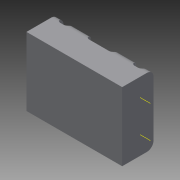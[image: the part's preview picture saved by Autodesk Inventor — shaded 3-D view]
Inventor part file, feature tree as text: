
AUTODESK INVENTOR PART (.ipt)
format: ipt  version: 2014 (Build 180170000, 170)  size: 228,864 bytes
history: native  units: mm
features: sketch x5, extrude x4, other x2, plane x1, fillet x1, shell x1, mirror x1
ambient origin geometry x8: Origin, YZ Plane, XZ Plane, XY Plane, X Axis, Y Axis, Z Axis, Center Point
bodies: Volumenkörper1 (feature_tree)
feature tree (15):
  extrude  "Extrusion1"  Depth=4.0mm
  plane  "Arbeitsebene1"
  fillet  "Rundung2"  Radius=19.0mm
  shell  "Hülle1"  Thickness=4.0mm
  extrude  "Extrusion2"  Depth=2.0mm
  mirror  "Spiegeln1"
  extrude  "Extrusion3"  Depth=2.0mm
  extrude  "Extrusion4"  Depth=2.0mm
  sketch  "Skizze5"  dims[d13=2.0mm d14=2.0mm d15=4.0mm d16=4.0mm d17=19.0mm d18=0.0mm d19=4.0mm d20=1.5mm d21=19.0mm d22=0.0mm]
  other  "Arbeitsachse1"
  other  "Arbeitsachse2"
  sketch  "Skizze1"  dims[d0=58.0mm d1=41.5mm d2=19.0mm d3=0.0mm d4=4.0mm]
  sketch  "Skizze2"  dims[d5=2.0mm d6=2.0mm]
  sketch  "Skizze3"  dims[d7=2.0mm d8=2.0mm]
  sketch  "Skizze4"  dims[d9=19.0mm d10=0.0mm d12=2.0mm]
